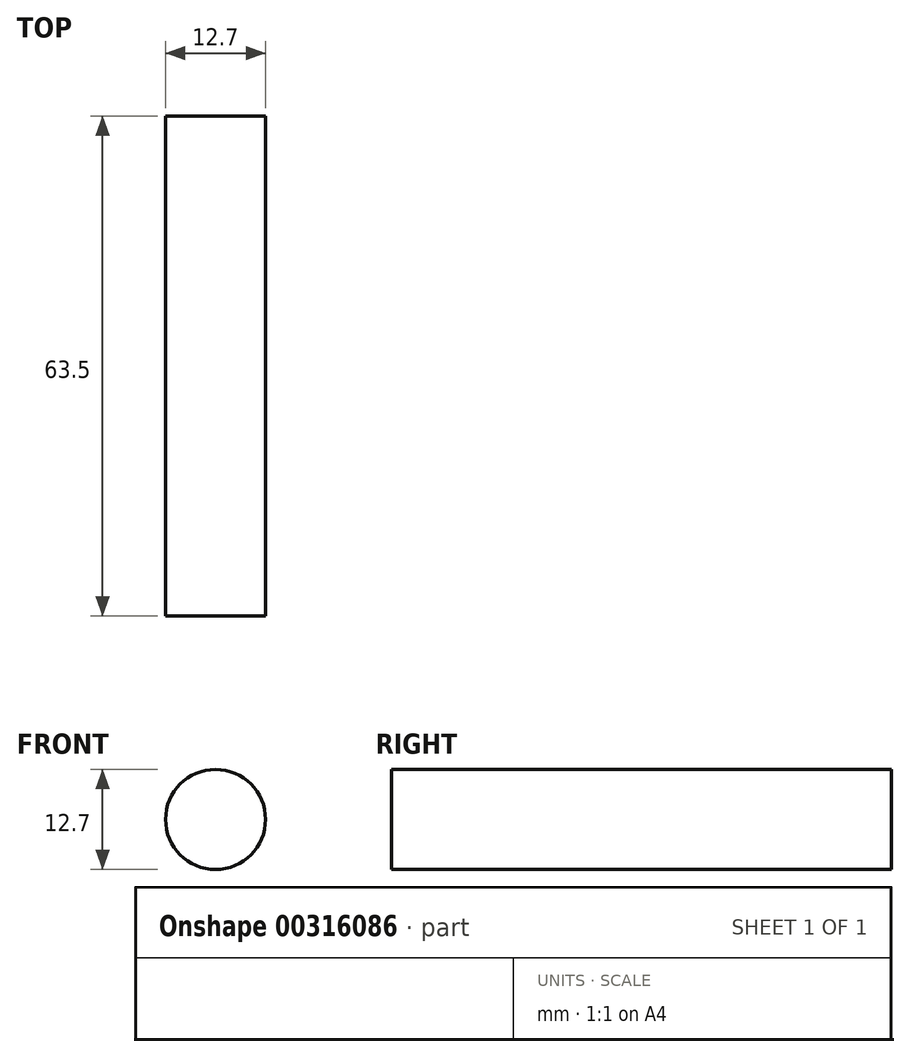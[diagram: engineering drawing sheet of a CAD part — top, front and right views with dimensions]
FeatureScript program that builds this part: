
annotation { "Feature Type Name" : "Feature", "Feature Type Description" : "" }
export const myFeature = defineFeature(function(context is Context, id is Id, definition is map)
    precondition{}
    {
        {
            var Q0;
            Q0=qCreatedBy(makeId("Front.planeOp"),FACE);
            var sketch = newSketch(context, id + "F0", { "sketchPlane" : qUnion([Q0])});
            skCircle(sketch, "E0", {"center": v(0, 0) * mm, "radius": 6.35 * mm});
            skSolve(sketch);
        }
        {
            var Q0;
            Q0=makeQuery(id+"F0.imprint","IMPRINT",FACE,{"disambiguationData":[TD([[makeQuery(id+"F0.imprint","IMPRINT",EDGE,{"derivedFrom":sQuery(id+"F0.wireOp",EDGE,"E0")}),1.0]])]});
            extrude(context, id + "F1", {"entities" : qUnion([Q0]), "depth" : 63.5 * mm});
        }
    });
